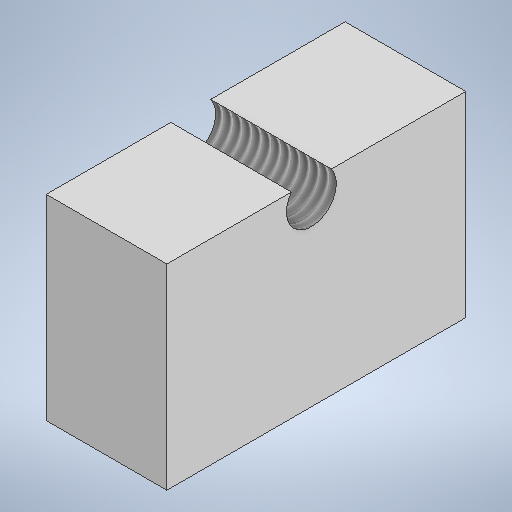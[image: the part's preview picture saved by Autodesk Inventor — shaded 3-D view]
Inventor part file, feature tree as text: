
AUTODESK INVENTOR PART (.ipt)
format: ipt  version: 2025.1 (Build 291241000, 241)  size: 203,264 bytes
history: native  units: mm
features: sketch x2, other x1, extrude x1, hole x1
ambient origin geometry x8: Origin, YZ Plane, XZ Plane, XY Plane, X Axis, Y Axis, Z Axis, Center Point
bodies: Body1 (feature_tree)
feature tree (5):
  other  "Sólido1"
  extrude  "Extrusión1"  Depth=10.0mm
  hole  "Agujero1"  [1 undecoded]
  sketch  "Boceto1"  dims[d0=10.0mm d1=0.0mm]
  sketch  "Boceto2"  dims[d2=4.134mm d3=10.0mm d4=4.0mm d5=2.0mm d6=90.0deg d7=8.0mm d8=20.594885mm d9=12.796864mm d10=15.0mm d11=0.0625mm d12=0.75mm d13=0.375mm]
note: 1 required parameter value undecoded (feature->parameter linkage not recoverable at this tier; creation-order binding heuristic only, values carry confidence <= 0.55)
